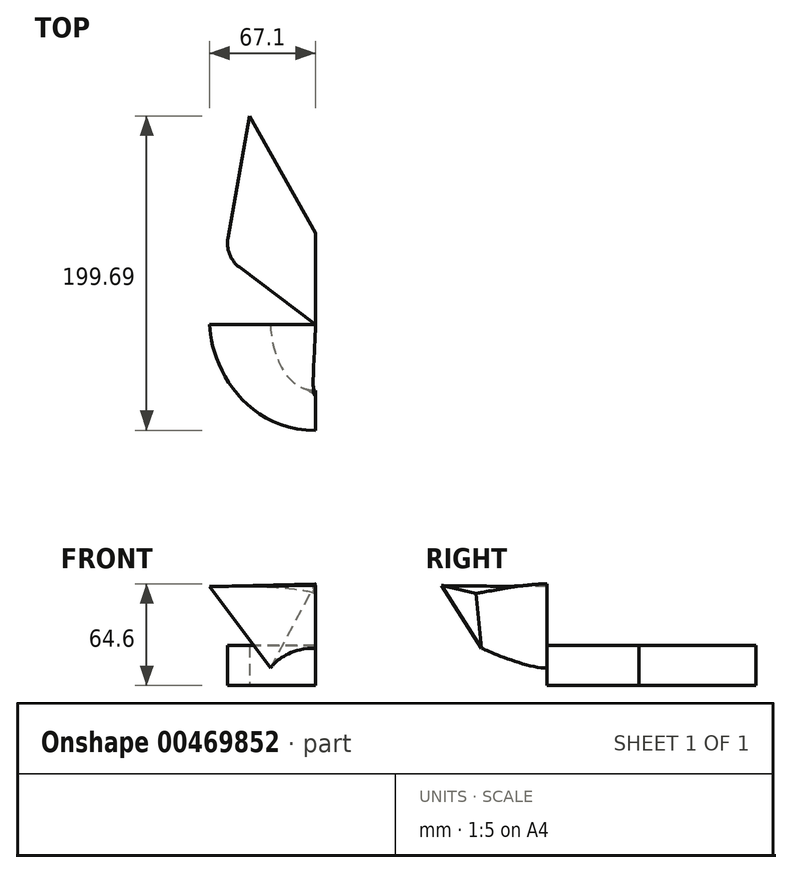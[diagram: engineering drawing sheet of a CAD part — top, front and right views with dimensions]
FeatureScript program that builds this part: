
annotation { "Feature Type Name" : "Feature", "Feature Type Description" : "" }
export const myFeature = defineFeature(function(context is Context, id is Id, definition is map)
    precondition{}
    {
        {
            var Q0;
            Q0=qCreatedBy(makeId("Top.planeOp"),FACE);
            var sketch = newSketch(context, id + "F0", { "sketchPlane" : qUnion([Q0])});
            skLineSegment(sketch, "E0", {"start": v(0, 0) * mm, "end": v(-48.29, 36.43) * mm});
            skLineSegment(sketch, "E1", {"start": v(-55.57, 54.94) * mm, "end": v(-41.91, 132.45) * mm});
            skLineSegment(sketch, "E2", {"start": v(-41.91, 132.45) * mm, "end": v(0, 58.14) * mm});
            skLineSegment(sketch, "E3", {"start": v(0, 58.14) * mm, "end": v(0, 0) * mm});
            skPoint(sketch, "E4.visualSharp", {"position": v(-57.6, 43.46) * mm});
            skArc(sketch, "E4.filletArc", {"start": v(-55.57, 54.94) * mm, "mid": v(-54.54, 44.66) * mm, "end": v(-48.29, 36.43) * mm});
            skSolve(sketch);
        }
        {
            var Q0;
            Q0 = qSketchRegion(id + "F0", true);
            extrude(context, id + "F1", {"entities" : qUnion([Q0]), "depth" : 25.4 * mm});
        }
        {
            var Q0;
            Q0=qCreatedBy(makeId("Front.planeOp"),FACE);
            var sketch = newSketch(context, id + "F2", { "sketchPlane" : qUnion([Q0])});
            skLineSegment(sketch, "E5", {"start": v(-67.1, 62.87) * mm, "end": v(-28.5, 11.07) * mm});
            skLineSegment(sketch, "E6", {"start": v(-28.5, 11.07) * mm, "end": v(0, 64.6) * mm});
            skLineSegment(sketch, "E7", {"start": v(0, 64.6) * mm, "end": v(-67.1, 62.87) * mm});
            skSolve(sketch);
        }
        {
            var Q0;
            Q0=qCreatedBy(makeId("Right.planeOp"),FACE);
            var sketch = newSketch(context, id + "F3", { "sketchPlane" : qUnion([Q0])});
            skLineSegment(sketch, "E8", {"start": v(-45.27, 58.4) * mm, "end": v(-67.24, 63.45) * mm});
            skLineSegment(sketch, "E9", {"start": v(-67.24, 63.45) * mm, "end": v(-41.85, 23.73) * mm});
            skLineSegment(sketch, "E10", {"start": v(-41.85, 23.73) * mm, "end": v(-45.27, 58.4) * mm});
            skSolve(sketch);
        }
        {
            var Q0;
            Q0=makeQuery(id+"F2.imprint","IMPRINT",FACE,{"disambiguationData":[TD([[makeQuery(id+"F2.imprint","IMPRINT",EDGE,{"derivedFrom":sQuery(id+"F2.wireOp",EDGE,"E5")}),1.0]])]});
            var Q1;
            Q1=makeQuery(id+"F3.imprint","IMPRINT",FACE,{"disambiguationData":[TD([[makeQuery(id+"F3.imprint","IMPRINT",EDGE,{"derivedFrom":sQuery(id+"F3.wireOp",EDGE,"E8")}),1.0]])]});
            loft(context, id + "F4", {"startCondition" : LoftEndDerivativeType.NORMAL_TO_PROFILE, "startMagnitude" : 1, "endCondition" : LoftEndDerivativeType.NORMAL_TO_PROFILE, "endMagnitude" : 2, "sheetProfilesArray" : [{ "sheetProfileEntities" : qUnion([Q0]) }, { "sheetProfileEntities" : qUnion([Q1]) }]});
        }
    });
